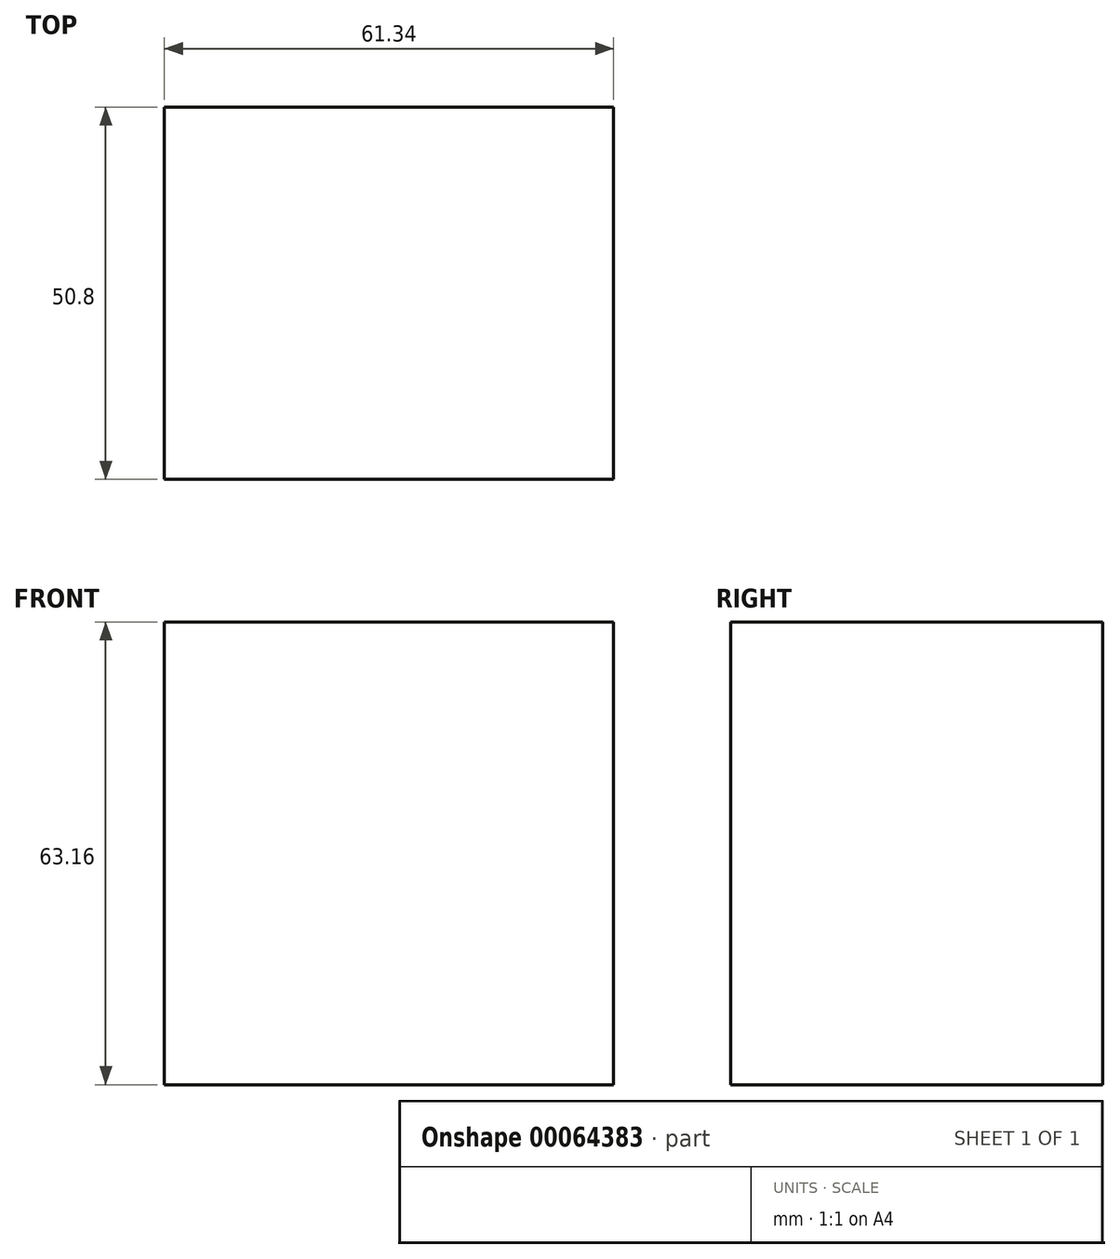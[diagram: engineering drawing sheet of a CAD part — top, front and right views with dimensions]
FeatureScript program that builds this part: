
annotation { "Feature Type Name" : "Feature", "Feature Type Description" : "" }
export const myFeature = defineFeature(function(context is Context, id is Id, definition is map)
    precondition{}
    {
        {
            var Q0;
            Q0=qCreatedBy(makeId("Front.planeOp"),FACE);
            var sketch = newSketch(context, id + "F0", { "sketchPlane" : qUnion([Q0])});
            skLineSegment(sketch, "E0.rect.bottom", {"start": v(-12.75, 11.08) * mm, "end": v(-74.09, 11.08) * mm});
            skLineSegment(sketch, "E0.rect.top", {"start": v(-12.75, 74.24) * mm, "end": v(-74.09, 74.24) * mm});
            skLineSegment(sketch, "E0.rect.left", {"start": v(-12.75, 11.08) * mm, "end": v(-12.75, 74.24) * mm});
            skLineSegment(sketch, "E0.rect.right", {"start": v(-74.09, 11.08) * mm, "end": v(-74.09, 74.24) * mm});
            skPoint(sketch, "E0.rect.middle", {"position": v(-43.42, 42.66) * mm});
            skSolve(sketch);
        }
        {
            var Q0;
            Q0 = qSketchRegion(id + "F0", true);
            extrude(context, id + "F1", {"entities" : qUnion([Q0]), "depth" : 50.8 * mm});
        }
    });
